# Revit family: EL-SL30024WW1HTN_()0000024630_Facebased_ver-2-0_2022____EL-X111W____
name_source: partatom
category: 照明器具
units: mm (PartAtom-declared; Revit-internal decimal feet)

## family parameters
パーツ タイプ = 標準
ホスト = 面
ロード時にボイドで切り取り = いいえ
丸型コネクタ寸法 = 直径を使用
光源 = はい
共有 = いいえ
注釈の向きを維持 = いいえ
部屋計算ポイント = いいえ

## types (2) — shared parameters
Height = 164  [stored 0.538058 ft]
IfcExportAs = IfcLightFixtureType
LED制御装置 = 一般形(LN)
URL = https://www.mitsubishielectric.co.jp
カラー フィルタ = 16777215
サービススペース = いいえ
モデル = EL-SL30024W/W 1HTN
ランプ_全光束 = 0 lm
ランプ_定格消費電力 = 0.0 W
ランプ_電流 = 0.000 A
レンダリング時に放射形状を表示 = はい
企業コード = 118713
保守率(1)良いのコメント = 保守率良いの場合：0.67
保守率(2)普通のコメント = 保守率普通の場合：0.63
保守率(3)悪いのコメント = 保守率悪いの場合：0.56
傾斜角 = -90.00°
入力電圧1(電圧指定=1) = 100 V
入力電圧2(電圧指定=2) = 0 V
入力電圧3(電圧指定=3) = 0 V
入力電流2 = 0.000 A
入力電流3 = 0.000 A
円の直径に沿って放射 = 98  [stored 0.321522 ft]
分類コード = 40300000000000
周波数 = 0 Hz
安定器_二次電圧 = 0 V
安定器_入力電力 = 0.0 W
安定器_入力電流 = 0.000 A
安定器_定格電圧 = 0 V
定格入力電圧 = 100 V
平均演色評価数(Ra) = 95
既定の高さ = 1219
材質_カバー = <カテゴリ別>
材質_ルーバー = <カテゴリ別>
材質_反射板 = <カテゴリ別>
材質_本体 = <カテゴリ別>
極数 = 1
消費電力2 = 0.0 W
消費電力3 = 0.0 W
直径 = 98  [stored 0.321522 ft]
相 = 1
積算_科目 = 1 電灯設備
製品質量 = 0.00 kg
製造元 = 三菱電機照明株式会社
設置方法 = 直付
調光ランプの色温度変化。 = <なし>
質量 = 0.00 kg
運転質量 = 0.00 kg
電圧指定 = 1
zero-valued in all types: Clearance Back, Clearance Bottom, Clearance Front, Clearance Left, Clearance Right, Clearance Top, Depth, Width, ランプ_定格消費効率(lm/W), ランプ_本数, 配光角, 開口部寸法(奥行), 開口部寸法(幅), 開口部寸法(径)

## per-type parameters (varying)
| type | コンバート開始日時 | フォトメトリック Web ファイル | 入力電流1 | 固有エネルギー消費効率(lm/W) | 定格光束 | 定格入力容量 | 定格入力電流 | 定格消費電力 | 消費電力1 | 皮相負荷 |
| _段調光_初期照度補正機能搭載なし_省電力（AK）_ | 2023年04月29日(土) 11時30分11秒983 | EL-SL30024WW1HTN_()0000024630___EL-X111W______DANCHO_-_SHODEN__.ies | 0.245 A | 89.711934 | 2180 lm | 25 VA | 0.245 A | 24.3 W | 24.3 W | 25 VA |
| _段調光_初期照度補正機能搭載なし_定格_ | 2023年04月29日(土) 11時30分09秒364 | EL-SL30024WW1HTN_()0000024625___EL-X111W______DANCHO_-_TEIKAKU__.ies | 0.326 A | 81.578947 | 2635 lm | 33 VA | 0.326 A | 32.3 W | 32.3 W | 33 VA |

note: [stored X ft] marks values corroborated as IEEE doubles in the binary element streams (Revit-internal decimal feet)
